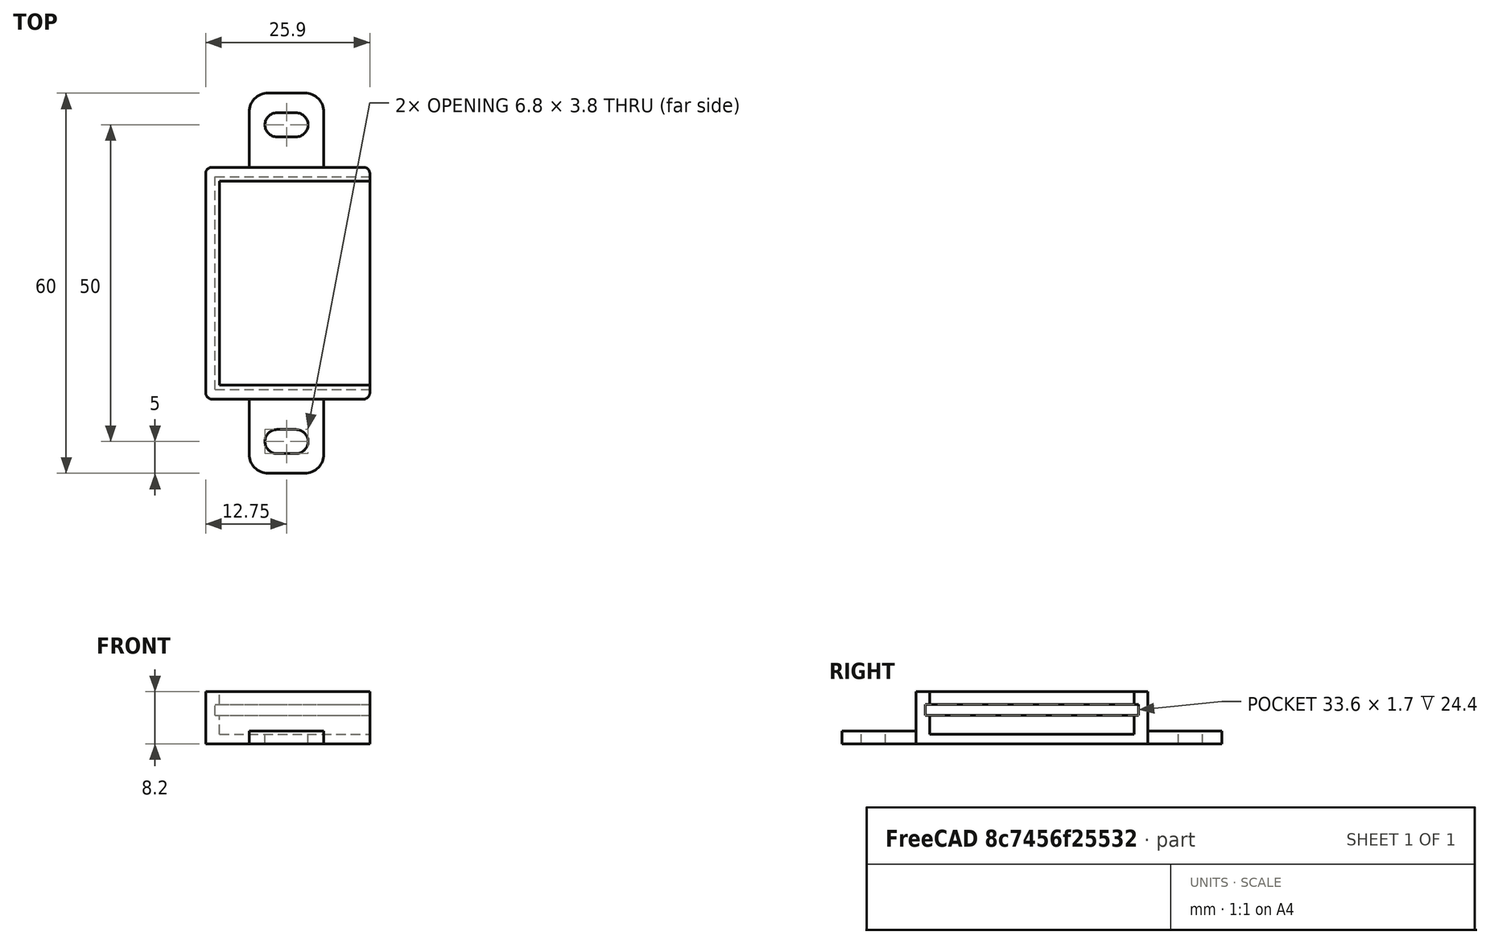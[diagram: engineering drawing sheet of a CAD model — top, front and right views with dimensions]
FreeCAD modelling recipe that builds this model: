
FCSTD DOCUMENT  (FreeCAD 0.19R)
Label: pcb_holder_slit_no_holes
License: FreeArt
LicenseURL: http://artlibre.org/licence/lal
objects: Part::Box×3, Part::MultiFuse×2, Spreadsheet::Sheet×1, Part::Fillet×1, Part::Feature×1, Part::Cut×1, App::Part×1
note: 8 computed .brp shape members not serialized (recipe doc carries the construction recipe); baked Part::Feature solids carry a one-line shape summary decoded from their .brp

FEATURE [Spreadsheet::Sheet] Spreadsheet  label="p"
  cells = A1=pcb_x; B1(pcb_x)=24.4; A2=pcb_y; B2(pcb_y)=33.6; A3=pcb_z; B3(pcb_z)=1.7; A4=pcb_under; B4(pcb_under)=3; A5=side_wall; B5(side_wall)=1.5; A6=pcb_side_lane; B6(pcb_side_lane)=0.7; A7=bottom_wall; B7(bottom_wall)=1.5; A8=pcb_above; B8(pcb_above)=2
FEATURE [Part::Box] Box  label="external cube"
  AttacherType = Attacher::AttachEngine3D
  Height = 8.2
  Length = 25.9
  Width = 36.6
  expr: Length = <<p>>.pcb_x + <<p>>.side_wall
  expr: Width = <<p>>.pcb_y + 2 * <<p>>.side_wall
  expr: Height = <<p>>.bottom_wall + <<p>>.pcb_under + <<p>>.pcb_z + <<p>>.pcb_above
FEATURE [Part::Box] Box006  label="internal cube"
  AttacherType = Attacher::AttachEngine3D
  Height = 6.7
  Length = 24.5
  Placement = pos=(2.2,2.2,1.5) rot=(0,0,1;0rad)
  Width = 32.2
  expr: Length = <<p>>.pcb_x - 2 * <<p>>.pcb_side_lane + <<p>>.side_wall
  expr: Width = <<p>>.pcb_y - 2 * <<p>>.pcb_side_lane
  expr: Height = <<p>>.pcb_under + <<p>>.pcb_z + <<p>>.pcb_above
  expr: .Placement.Base.z = <<p>>.bottom_wall
  expr: .Placement.Base.x = <<p>>.side_wall + <<p>>.pcb_side_lane
  expr: .Placement.Base.y = <<p>>.side_wall + <<p>>.pcb_side_lane
FEATURE [Part::Box] Box007  label="pcb extract cube"
  AttacherType = Attacher::AttachEngine3D
  Height = 1.7
  Length = 24.4
  Placement = pos=(1.5,1.5,4.5) rot=(0,0,1;0rad)
  Width = 33.6
  expr: Height = <<p>>.pcb_z
  expr: .Placement.Base.z = <<p>>.bottom_wall + <<p>>.pcb_under
  expr: Width = <<p>>.pcb_y
  expr: Length = <<p>>.pcb_x
  expr: .Placement.Base.x = <<p>>.side_wall
  expr: .Placement.Base.y = <<p>>.side_wall
FEATURE [Part::MultiFuse] Fusion  label="extract fusion"
  Shapes = -> [Box006,Box007]
FEATURE [Part::Fillet] Fillet  label="external fillet"
  Base = -> Box
  Edges = 4 edges r=1: [Edge1,Edge3,Edge5,Edge7]
FEATURE [Part::Feature] Cut002001  label="attach plane y dir001"
  Placement = pos=(6.85,-11.7,0) rot=(0,0,1;0rad)
  shape: bbox 11.8 x 60 x 2 mm, 20 faces (baked)
FEATURE [Part::MultiFuse] Fusion001  label="solid fusion"
  Shapes = -> [Fillet,Cut002001]
FEATURE [Part::Cut] Cut  label="body cut"
  Base = -> Fusion001
  Tool = -> Fusion
FEATURE [App::Part] Part  label="charger hw pcb box part"
  Group = -> [Box,Fillet,Fusion001,Fusion,Box007,Box006,Cut]
  Origin = -> Origin
